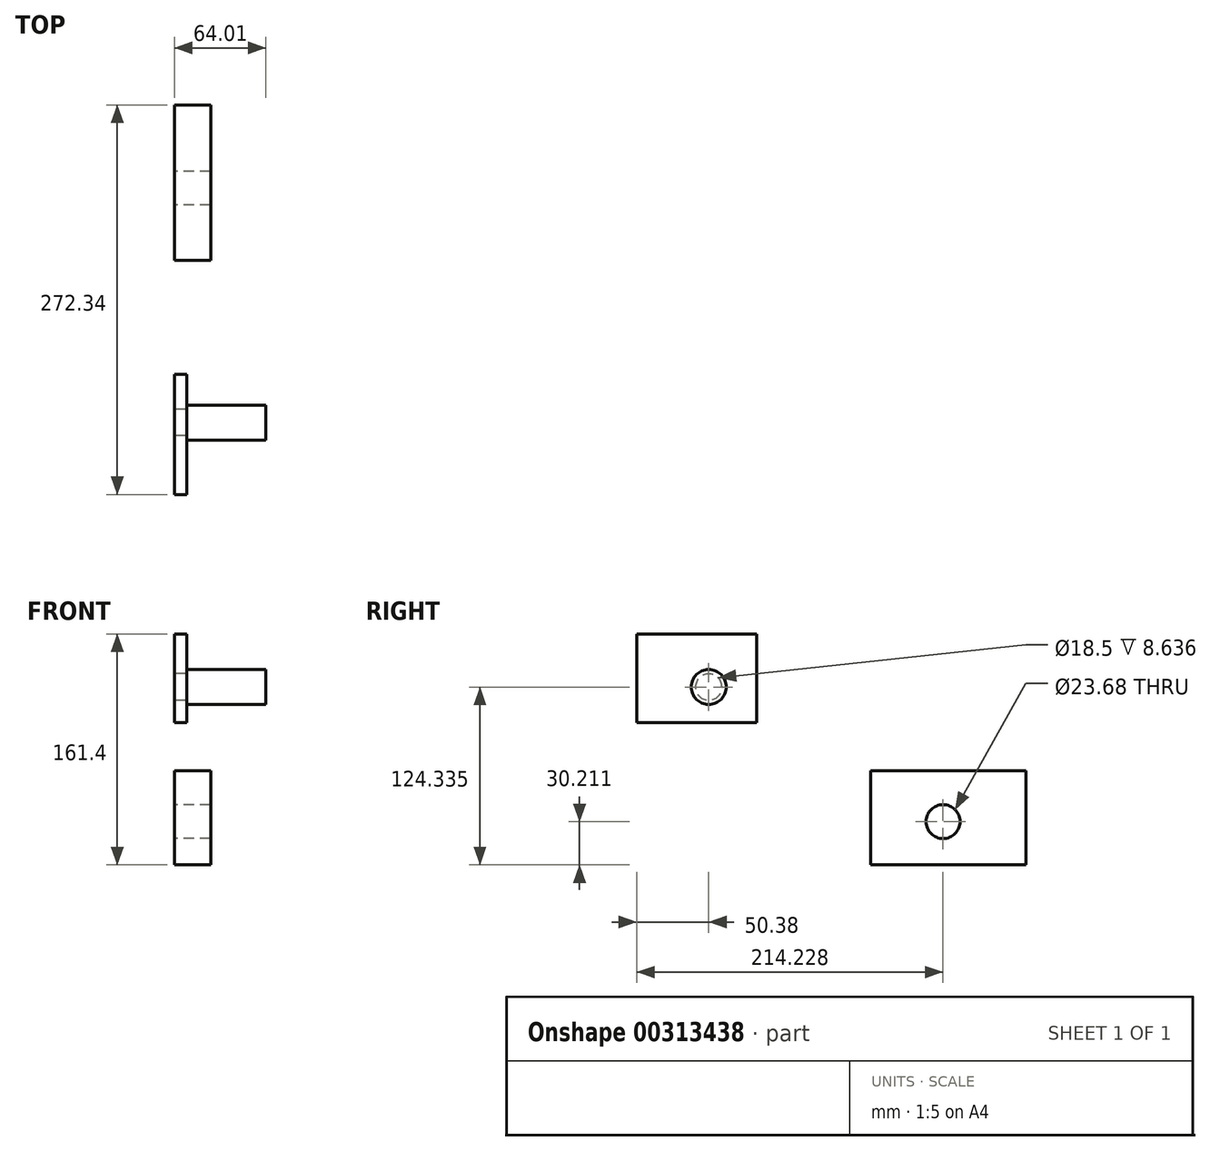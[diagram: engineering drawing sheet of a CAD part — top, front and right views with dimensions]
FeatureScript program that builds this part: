
annotation { "Feature Type Name" : "Feature", "Feature Type Description" : "" }
export const myFeature = defineFeature(function(context is Context, id is Id, definition is map)
    precondition{}
    {
        {
            var Q0;
            Q0=qCreatedBy(makeId("Right.planeOp"),FACE);
            var sketch = newSketch(context, id + "F0", { "sketchPlane" : qUnion([Q0])});
            skCircle(sketch, "E0", {"center": v(0, 0) * mm, "radius": 14.68 * mm});
            skSolve(sketch);
        }
        {
            var Q0;
            Q0=sQuery(id+"F0.wireOp",EDGE,"E0");
            extrude(context, id + "F1", {"bodyType" : ToolBodyType.SURFACE, "surfaceEntities" : qUnion([Q0]), "depth" : 91.95 * mm});
        }
        {
            var Q0;
            Q0=qCreatedBy(makeId("Right.planeOp"),FACE);
            var sketch = newSketch(context, id + "F2", { "sketchPlane" : qUnion([Q0])});
            skLineSegment(sketch, "E1.bottom", {"start": v(-50.38, 40.05) * mm, "end": v(33.62, 40.05) * mm});
            skLineSegment(sketch, "E1.top", {"start": v(-50.38, -21.9) * mm, "end": v(33.62, -21.9) * mm});
            skLineSegment(sketch, "E1.left", {"start": v(-50.38, 40.05) * mm, "end": v(-50.38, -21.9) * mm});
            skLineSegment(sketch, "E1.right", {"start": v(33.62, 40.05) * mm, "end": v(33.62, -21.9) * mm});
            skSolve(sketch);
        }
        {
            var Q0;
            Q0=makeQuery(id+"F2.imprint","IMPRINT",FACE,{"disambiguationData":[TD([[makeQuery(id+"F2.imprint","IMPRINT",EDGE,{"derivedFrom":sQuery(id+"F2.wireOp",EDGE,"E1.bottom")}),-1.0]])]});
            var sketch = newSketch(context, id + "F3", { "sketchPlane" : qUnion([Q0])});
            skCircle(sketch, "E2", {"center": v(0, 2.99) * mm, "radius": 9.25 * mm});
            skSolve(sketch);
        }
        {
            var Q0;
            Q0=makeQuery(id+"F3.imprint","IMPRINT",FACE,{"disambiguationData":[TD([[makeQuery(id+"F3.imprint","IMPRINT",EDGE,{"derivedFrom":sQuery(id+"F3.wireOp",EDGE,"E2")}),-1.0]])]});
            extrude(context, id + "F4", {"entities" : qUnion([Q0]), "depth" : 8.64 * mm});
        }
        {
            var Q0;
            Q0=makeQuery(id+"F4.opExtrude","CAP_FACE",FACE,{"disambiguationData":[OSD([sQuery(id+"F2.wireOp",EDGE,"E1.bottom"),sQuery(id+"F2.wireOp",EDGE,"E1.top"),sQuery(id+"F2.wireOp",EDGE,"E1.left"),sQuery(id+"F2.wireOp",EDGE,"E1.right"),sQuery(id+"F3.wireOp",EDGE,"E2")])],"isStart":false});
            var sketch = newSketch(context, id + "F5", { "sketchPlane" : qUnion([Q0])});
            skCircle(sketch, "E3", {"center": v(0, 2.99) * mm, "radius": 12.22 * mm});
            skSolve(sketch);
        }
        {
            var Q0;
            Q0 = qSketchRegion(id + "F5", true);
            extrude(context, id + "F6", {"entities" : qUnion([Q0]), "operationType" : NewBodyOperationType.ADD, "depth" : 55.37 * mm});
        }
        {
            var Q0;
            Q0=qCreatedBy(makeId("Right.planeOp"),FACE);
            var sketch = newSketch(context, id + "F7", { "sketchPlane" : qUnion([Q0])});
            skLineSegment(sketch, "E4.bottom", {"start": v(113.25, -55.43) * mm, "end": v(221.96, -55.43) * mm});
            skLineSegment(sketch, "E4.top", {"start": v(113.25, -121.35) * mm, "end": v(221.96, -121.35) * mm});
            skLineSegment(sketch, "E4.left", {"start": v(113.25, -55.43) * mm, "end": v(113.25, -121.35) * mm});
            skLineSegment(sketch, "E4.right", {"start": v(221.96, -55.43) * mm, "end": v(221.96, -121.35) * mm});
            skCircle(sketch, "E5", {"center": v(163.85, -91.14) * mm, "radius": 11.84 * mm});
            skSolve(sketch);
        }
        {
            var Q0;
            Q0 = qSketchRegion(id + "F7", true);
            extrude(context, id + "F8", {"entities" : qUnion([Q0]), "depth" : 25.4 * mm});
        }
    });
